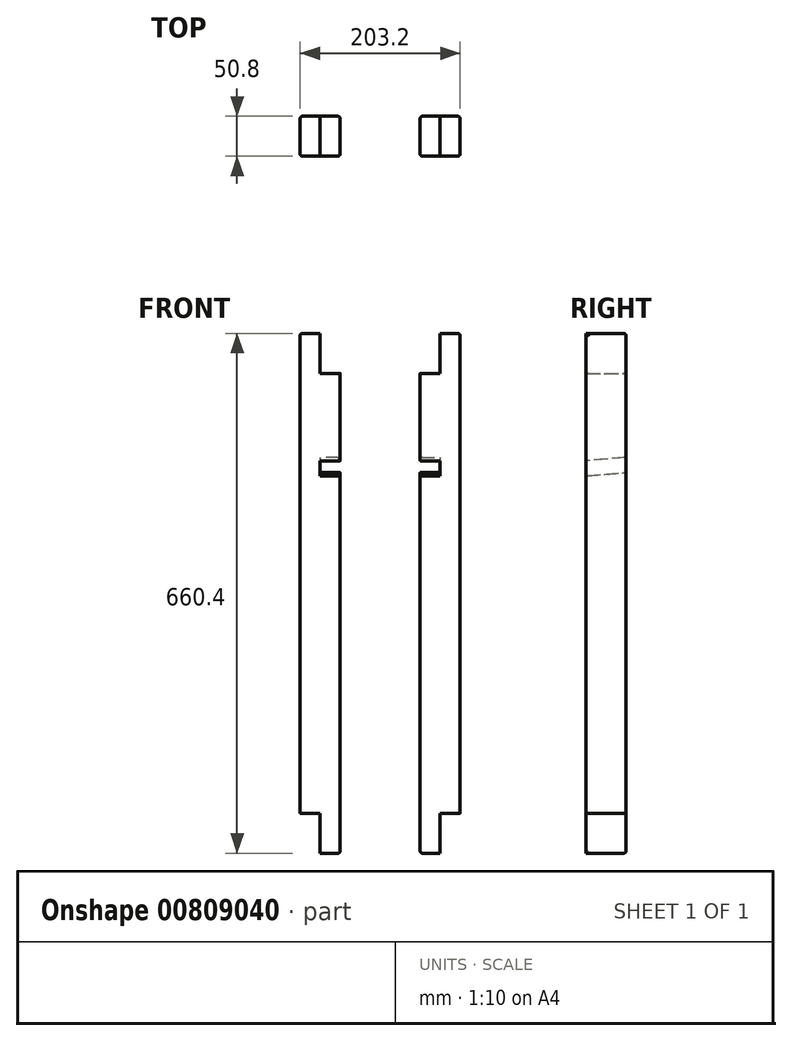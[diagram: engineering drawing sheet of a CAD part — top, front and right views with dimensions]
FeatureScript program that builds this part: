
annotation { "Feature Type Name" : "Feature", "Feature Type Description" : "" }
export const myFeature = defineFeature(function(context is Context, id is Id, definition is map)
    precondition{}
    {
        {
            var Q0;
            Q0=qCreatedBy(makeId("Top.planeOp"),FACE);
            var sketch = newSketch(context, id + "F0", { "sketchPlane" : qUnion([Q0])});
            skLineSegment(sketch, "E0.bottom", {"start": v(0, 0) * mm, "end": v(25.4, 0) * mm});
            skLineSegment(sketch, "E0.top", {"start": v(0, 50.8) * mm, "end": v(25.4, 50.8) * mm});
            skLineSegment(sketch, "E0.left", {"start": v(0, 0) * mm, "end": v(0, 50.8) * mm});
            skLineSegment(sketch, "E0.right", {"start": v(25.4, 0) * mm, "end": v(25.4, 50.8) * mm});
            skLineSegment(sketch, "E1.bottom", {"start": v(0, 0) * mm, "end": v(-25.4, 0) * mm});
            skLineSegment(sketch, "E1.top", {"start": v(0, 50.8) * mm, "end": v(-25.4, 50.8) * mm});
            skLineSegment(sketch, "E1.right", {"start": v(-25.4, 0) * mm, "end": v(-25.4, 50.8) * mm});
            skSolve(sketch);
        }
        {
            var Q0;
            Q0=makeQuery(id+"F0.imprint","IMPRINT",FACE,{"disambiguationData":[TD([[makeQuery(id+"F0.imprint","IMPRINT",EDGE,{"derivedFrom":sQuery(id+"F0.wireOp",EDGE,"E0.bottom")}),1.0]])]});
            extrude(context, id + "F1", {"entities" : qUnion([Q0]), "depth" : 609.6 * mm, "offsetDistance" : 25.4 * mm});
        }
        {
            var Q0;
            Q0=makeQuery(id+"F0.imprint","IMPRINT",FACE,{"disambiguationData":[TD([[makeQuery(id+"F0.imprint","IMPRINT",EDGE,{"derivedFrom":sQuery(id+"F0.wireOp",EDGE,"E1.bottom")}),-1.0]])]});
            extrude(context, id + "F2", {"entities" : qUnion([Q0]), "operationType" : NewBodyOperationType.ADD, "oppositeDirection" : true, "depth" : 50.8 * mm, "offsetDistance" : 25.4 * mm, "hasSecondDirection" : true, "secondDirectionOppositeDirection" : false, "secondDirectionDepth" : 558.8 * mm});
        }
        {
            var Q0;
            Q0=qCreatedBy(makeId("Right.planeOp"),FACE);
            var sketch = newSketch(context, id + "F3", { "sketchPlane" : qUnion([Q0])});
            skLineSegment(sketch, "E2", {"start": v(50.8, 432.97) * mm, "end": v(50.8, 452.1) * mm});
            skLineSegment(sketch, "E3", {"start": v(50.8, 452.1) * mm, "end": v(0, 447.65) * mm});
            skLineSegment(sketch, "E4", {"start": v(0, 447.65) * mm, "end": v(0, 428.52) * mm});
            skLineSegment(sketch, "E5", {"start": v(0, 428.52) * mm, "end": v(50.8, 432.97) * mm});
            skSolve(sketch);
        }
        {
            var Q0;
            Q0 = qSketchRegion(id + "F3", true);
            extrude(context, id + "F4", {"entities" : qUnion([Q0]), "operationType" : NewBodyOperationType.REMOVE, "oppositeDirection" : true, "depth" : 25.4 * mm, "offsetDistance" : 25.4 * mm});
        }
        {
            var Q0;
            {var subQ0=sQuery(id+"F0.wireOp",EDGE,"E1.right");var subQ1=sQuery(id+"F0.wireOp",EDGE,"E1.top");Q0=makeQuery(id+"F4.boolean.opBoolean","SPLIT",EDGE,{"disambiguationData":[TD([makeQuery(id+"F4.opExtrude","SWEPT_FACE",FACE,{"disambiguationData":[OSD([sQuery(id+"F3.wireOp",EDGE,"E3")])]})])],"derivedFrom":makeQuery(id+"F2.opExtrude","SWEPT_EDGE",EDGE,{"disambiguationData":[OSD([subQ1,subQ0])]})});}
            var Q1;
            {var subQ0=sQuery(id+"F0.wireOp",EDGE,"E1.right");var subQ1=sQuery(id+"F0.wireOp",EDGE,"E1.bottom");Q1=makeQuery(id+"F4.boolean.opBoolean","SPLIT",EDGE,{"disambiguationData":[TD([makeQuery(id+"F4.opExtrude","SWEPT_FACE",FACE,{"disambiguationData":[OSD([sQuery(id+"F3.wireOp",EDGE,"E3")])]})])],"derivedFrom":makeQuery(id+"F2.opExtrude","SWEPT_EDGE",EDGE,{"disambiguationData":[OSD([subQ1,subQ0])]})});}
            var Q2;
            {var subQ0=sQuery(id+"F0.wireOp",EDGE,"E1.right");var subQ1=sQuery(id+"F0.wireOp",EDGE,"E1.top");Q2=makeQuery(id+"F4.boolean.opBoolean","SPLIT",EDGE,{"disambiguationData":[TD([makeQuery(id+"F4.opExtrude","SWEPT_FACE",FACE,{"disambiguationData":[OSD([sQuery(id+"F3.wireOp",EDGE,"E5")])]})])],"derivedFrom":makeQuery(id+"F2.opExtrude","SWEPT_EDGE",EDGE,{"disambiguationData":[OSD([subQ1,subQ0])]})});}
            var Q3;
            {var subQ0=sQuery(id+"F0.wireOp",EDGE,"E1.right");var subQ1=sQuery(id+"F0.wireOp",EDGE,"E1.bottom");Q3=makeQuery(id+"F4.boolean.opBoolean","SPLIT",EDGE,{"disambiguationData":[TD([makeQuery(id+"F4.opExtrude","SWEPT_FACE",FACE,{"disambiguationData":[OSD([sQuery(id+"F3.wireOp",EDGE,"E5")])]})])],"derivedFrom":makeQuery(id+"F2.opExtrude","SWEPT_EDGE",EDGE,{"disambiguationData":[OSD([subQ1,subQ0])]})});}
            var Q4;
            Q4=makeQuery(id+"F1.opExtrude","CAP_EDGE",EDGE,{"disambiguationData":[OSD([sQuery(id+"F0.wireOp",EDGE,"E0.top")])],"isStart":false});
            var Q5;
            Q5=makeQuery(id+"F1.opExtrude","CAP_EDGE",EDGE,{"disambiguationData":[OSD([sQuery(id+"F0.wireOp",EDGE,"E0.right")])],"isStart":false});
            var Q6;
            Q6=makeQuery(id+"F1.opExtrude","SWEPT_EDGE",EDGE,{"disambiguationData":[OSD([sQuery(id+"F0.wireOp",EDGE,"E0.top"),sQuery(id+"F0.wireOp",EDGE,"E0.right")])]});
            var Q7;
            Q7=makeQuery(id+"F1.opExtrude","SWEPT_EDGE",EDGE,{"disambiguationData":[OSD([sQuery(id+"F0.wireOp",EDGE,"E0.bottom"),sQuery(id+"F0.wireOp",EDGE,"E0.right")])]});
            var Q8;
            Q8=makeQuery(id+"F2.opExtrude","CAP_EDGE",EDGE,{"disambiguationData":[OSD([sQuery(id+"F0.wireOp",EDGE,"E1.right")])],"isStart":false});
            var Q9;
            Q9=makeQuery(id+"F2.opExtrude","CAP_EDGE",EDGE,{"disambiguationData":[OSD([sQuery(id+"F0.wireOp",EDGE,"E1.top")])],"isStart":false});
            fillet(context, id + "F5", {"entities" : qUnion([Q0, Q1, Q2, Q3, Q4, Q5, Q6, Q7, Q8, Q9]), "radius" : 3.17 * mm, "tangentPropagation" : true, "allowEdgeOverflow" : false});
        }
        {
            var Q0;
            Q0=qCreatedBy(makeId("Right.planeOp"),FACE);
            cPlane(context, id + "F6", {"entities" : qUnion([Q0]), "cplaneType" : CPlaneType.OFFSET, "offset" : 76.2 * mm, "oppositeDirection" : true, "width" : 152.4 * mm, "height" : 152.4 * mm});
        }
        {
            var Q0;
            Q0=makeQuery(id+"F1.opExtrude","SWEPT_BODY",BODY,{"disambiguationData":[OSD([sQuery(id+"F0.wireOp",EDGE,"E0.bottom"),sQuery(id+"F0.wireOp",EDGE,"E0.top"),sQuery(id+"F0.wireOp",EDGE,"E0.right"),sQuery(id+"F0.wireOp",EDGE,"E0.left")])]});
            var Q1;
            Q1=qCreatedBy(id+"F6.planeOp",FACE);
            mirror(context, id + "F7", {"entities" : qUnion([Q0]), "mirrorPlane" : qUnion([Q1])});
        }
    });
